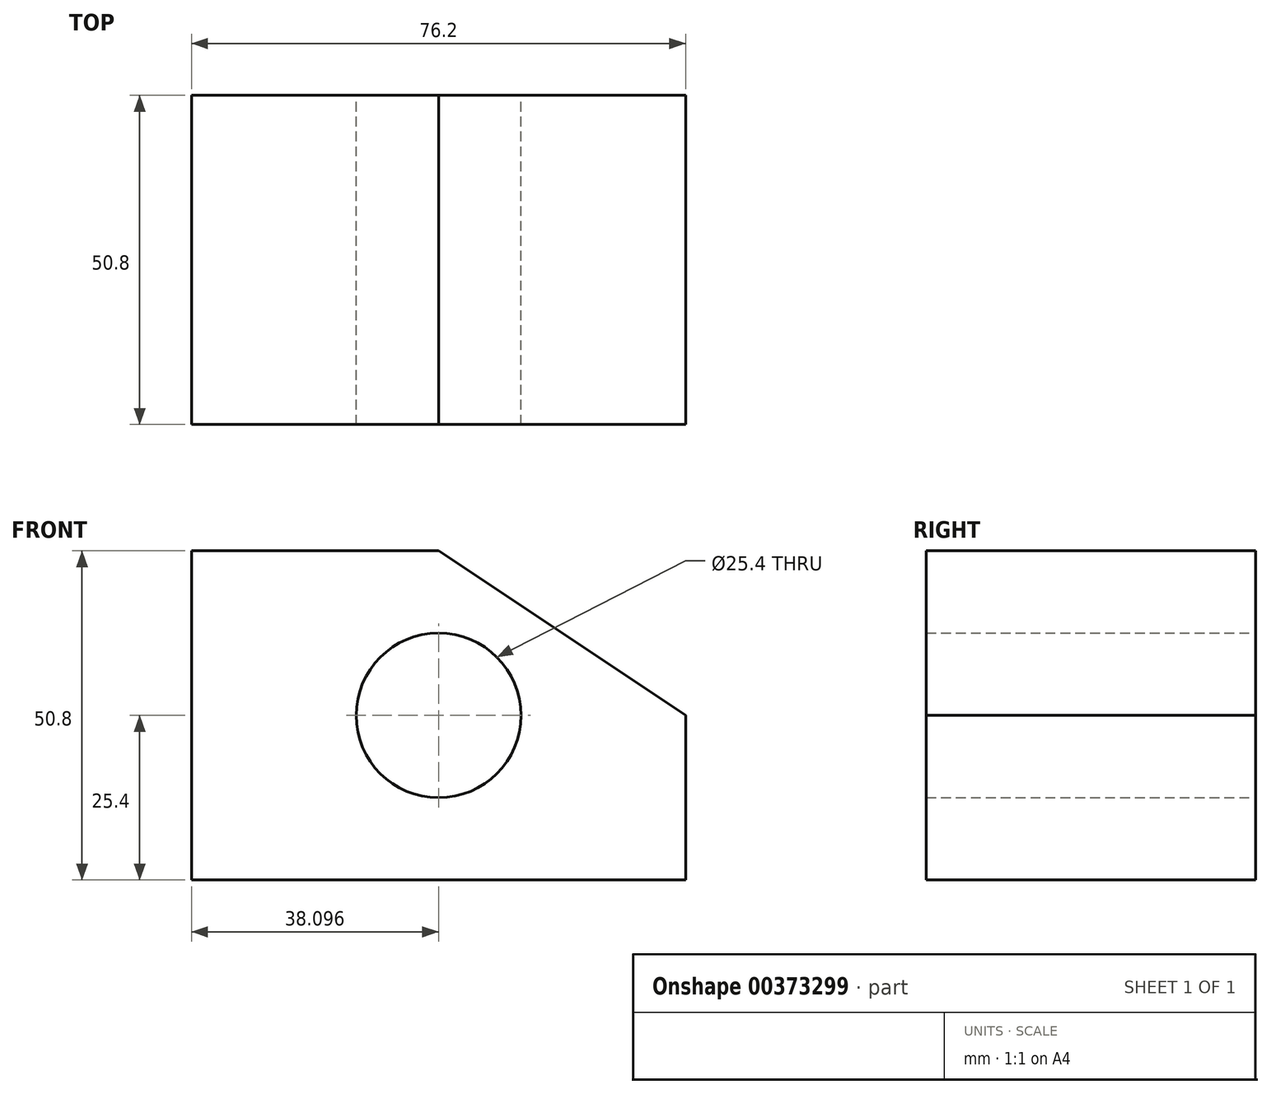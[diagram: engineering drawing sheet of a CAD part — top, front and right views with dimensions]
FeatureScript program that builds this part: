
annotation { "Feature Type Name" : "Feature", "Feature Type Description" : "" }
export const myFeature = defineFeature(function(context is Context, id is Id, definition is map)
    precondition{}
    {
        {
            var Q0;
            Q0=qCreatedBy(makeId("Front.planeOp"),FACE);
            var sketch = newSketch(context, id + "F0", { "sketchPlane" : qUnion([Q0])});
            skLineSegment(sketch, "E0", {"start": v(-49.32, 39.8) * mm, "end": v(-49.32, -11) * mm});
            skLineSegment(sketch, "E1", {"start": v(-49.32, -11) * mm, "end": v(26.88, -11) * mm});
            skLineSegment(sketch, "E2", {"start": v(26.88, -11) * mm, "end": v(26.88, 14.4) * mm});
            skLineSegment(sketch, "E3", {"start": v(-49.32, 39.8) * mm, "end": v(-11.22, 39.8) * mm});
            skLineSegment(sketch, "E4", {"start": v(-11.22, 39.8) * mm, "end": v(26.88, 14.4) * mm});
            skPoint(sketch, "E5", {"position": v(-11.22, 14.4) * mm});
            skPoint(sketch, "E6", {"position": v(108.21, 57.56) * mm});
            skCircle(sketch, "E7", {"center": v(-11.22, 14.4) * mm, "radius": 12.7 * mm});
            skSolve(sketch);
        }
        {
            var Q0;
            Q0=makeQuery(id+"F0.imprint","IMPRINT",FACE,{"disambiguationData":[TD([[makeQuery(id+"F0.imprint","IMPRINT",EDGE,{"derivedFrom":sQuery(id+"F0.wireOp",EDGE,"E0")}),1.0]])]});
            extrude(context, id + "F1", {"entities" : qUnion([Q0]), "depth" : 50.8 * mm});
        }
    });
